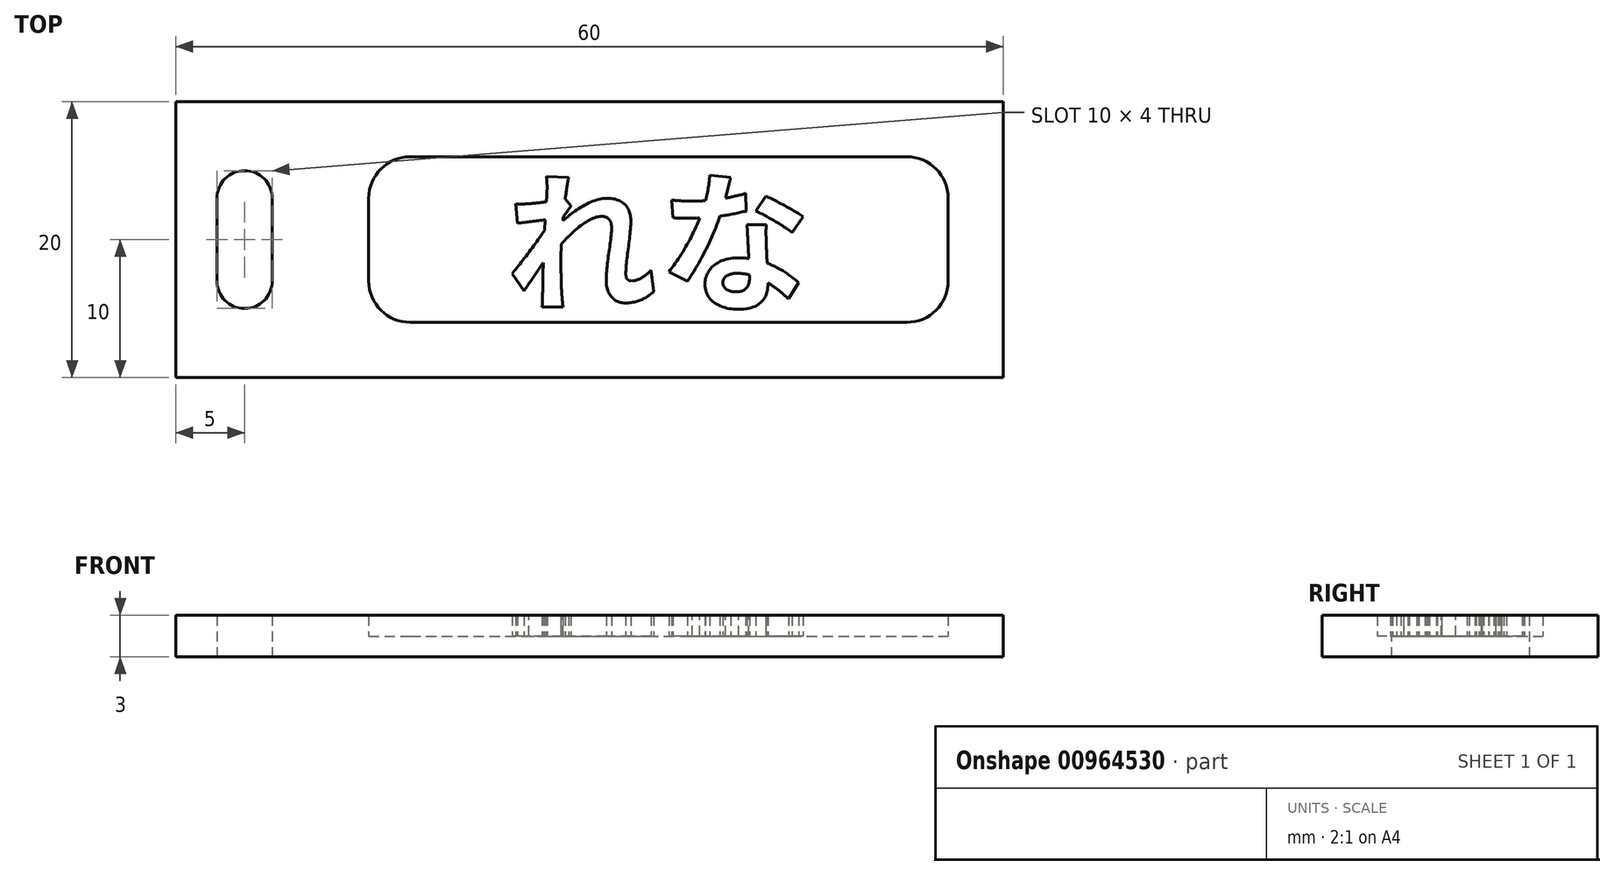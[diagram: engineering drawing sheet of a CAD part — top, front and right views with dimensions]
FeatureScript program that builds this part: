
annotation { "Feature Type Name" : "Feature", "Feature Type Description" : "" }
export const myFeature = defineFeature(function(context is Context, id is Id, definition is map)
    precondition{}
    {
        {
            var Q0;
            Q0=qCreatedBy(makeId("Top.planeOp"),FACE);
            var sketch = newSketch(context, id + "F0", { "sketchPlane" : qUnion([Q0])});
            skLineSegment(sketch, "E0.bottom", {"start": v(-25, 10) * mm, "end": v(25, 10) * mm});
            skLineSegment(sketch, "E0.top", {"start": v(-25, -10) * mm, "end": v(25, -10) * mm});
            skLineSegment(sketch, "E0.left", {"start": v(-25, 10) * mm, "end": v(-25, -10) * mm});
            skLineSegment(sketch, "E0.right", {"start": v(25, 10) * mm, "end": v(25, -10) * mm});
            skPoint(sketch, "E0.middle", {"position": v(0, 0) * mm});
            skLineSegment(sketch, "E1.bottom", {"start": v(-25, 10) * mm, "end": v(-35, 10) * mm});
            skLineSegment(sketch, "E1.top", {"start": v(-25, -10) * mm, "end": v(-35, -10) * mm});
            skLineSegment(sketch, "E1.right", {"start": v(-35, 10) * mm, "end": v(-35, -10) * mm});
            skPoint(sketch, "E1.middle", {"position": v(-30, 0) * mm});
            skLineSegment(sketch, "E2.bottom", {"start": v(-30, 5) * mm, "end": v(-30, 5) * mm});
            skLineSegment(sketch, "E2.top", {"start": v(-30, -5) * mm, "end": v(-30, -5) * mm});
            skLineSegment(sketch, "E2.left", {"start": v(-32, 3) * mm, "end": v(-32, -3) * mm});
            skLineSegment(sketch, "E2.right", {"start": v(-28, 3) * mm, "end": v(-28, -3) * mm});
            skPoint(sketch, "E3.visualSharp", {"position": v(-32, 5) * mm});
            skArc(sketch, "E3.filletArc", {"start": v(-30, 5) * mm, "mid": v(-31.41, 4.41) * mm, "end": v(-32, 3) * mm});
            skPoint(sketch, "E4.visualSharp", {"position": v(-28, 5) * mm});
            skArc(sketch, "E4.filletArc", {"start": v(-28, 3) * mm, "mid": v(-28.59, 4.41) * mm, "end": v(-30, 5) * mm});
            skPoint(sketch, "E5.visualSharp", {"position": v(-28, -5) * mm});
            skArc(sketch, "E5.filletArc", {"start": v(-30, -5) * mm, "mid": v(-28.59, -4.41) * mm, "end": v(-28, -3) * mm});
            skPoint(sketch, "E6.visualSharp", {"position": v(-32, -5) * mm});
            skArc(sketch, "E6.filletArc", {"start": v(-32, -3) * mm, "mid": v(-31.41, -4.41) * mm, "end": v(-30, -5) * mm});
            skSolve(sketch);
        }
        {
            var Q0;
            Q0 = qSketchRegion(id + "F0", true);
            extrude(context, id + "F1", {"entities" : qUnion([Q0]), "depth" : 3 * mm, "offsetDistance" : 25 * mm});
        }
        {
            var Q0;
            Q0=qCreatedBy(makeId("Top.planeOp"),FACE);
            var sketch = newSketch(context, id + "F2", { "sketchPlane" : qUnion([Q0])});
            skLineSegment(sketch, "E7.bottom", {"start": v(-18, -6) * mm, "end": v(18, -6) * mm});
            skLineSegment(sketch, "E7.top", {"start": v(-18, 6) * mm, "end": v(18, 6) * mm});
            skLineSegment(sketch, "E7.left", {"start": v(-21, -3) * mm, "end": v(-21, 3) * mm});
            skLineSegment(sketch, "E7.right", {"start": v(21, -3) * mm, "end": v(21, 3) * mm});
            skPoint(sketch, "E7.middle", {"position": v(0, 0) * mm});
            skPoint(sketch, "E8.visualSharp", {"position": v(-21, 6) * mm});
            skArc(sketch, "E8.filletArc", {"start": v(-18, 6) * mm, "mid": v(-20.12, 5.12) * mm, "end": v(-21, 3) * mm});
            skPoint(sketch, "E9.visualSharp", {"position": v(-21, -6) * mm});
            skArc(sketch, "E9.filletArc", {"start": v(-21, -3) * mm, "mid": v(-20.12, -5.12) * mm, "end": v(-18, -6) * mm});
            skPoint(sketch, "E10.visualSharp", {"position": v(21, -6) * mm});
            skArc(sketch, "E10.filletArc", {"start": v(18, -6) * mm, "mid": v(20.12, -5.12) * mm, "end": v(21, -3) * mm});
            skPoint(sketch, "E11.visualSharp", {"position": v(21, 6) * mm});
            skArc(sketch, "E11.filletArc", {"start": v(21, 3) * mm, "mid": v(20.12, 5.12) * mm, "end": v(18, 6) * mm});
            skSolve(sketch);
        }
        {
            var Q0;
            Q0 = qSketchRegion(id + "F2", true);
            extrude(context, id + "F3", {"entities" : qUnion([Q0]), "depth" : 3 * mm, "offsetDistance" : 25 * mm});
        }
        {
            var Q0;
            Q0=makeQuery(id+"F3.opExtrude","SWEPT_BODY",BODY,{"disambiguationData":[OSD([sQuery(id+"F2.wireOp",EDGE,"E7.bottom"),sQuery(id+"F2.wireOp",EDGE,"E7.top"),sQuery(id+"F2.wireOp",EDGE,"E7.left"),sQuery(id+"F2.wireOp",EDGE,"E7.right"),sQuery(id+"F2.wireOp",EDGE,"E8.filletArc"),sQuery(id+"F2.wireOp",EDGE,"E9.filletArc"),sQuery(id+"F2.wireOp",EDGE,"E10.filletArc"),sQuery(id+"F2.wireOp",EDGE,"E11.filletArc")])]});
            transform(context, id + "F4", {"entities" : qUnion([Q0]), "transformType" : TransformType.TRANSLATION_3D, "dx" : 0 * mm, "dy" : 0 * mm, "dz" : 1.5 * mm, "makeCopy" : false});
        }
        {
            var Q0;
            Q0=makeQuery(id+"F3.opExtrude","SWEPT_BODY",BODY,{"disambiguationData":[OSD([sQuery(id+"F2.wireOp",EDGE,"E7.bottom"),sQuery(id+"F2.wireOp",EDGE,"E7.top"),sQuery(id+"F2.wireOp",EDGE,"E7.left"),sQuery(id+"F2.wireOp",EDGE,"E7.right"),sQuery(id+"F2.wireOp",EDGE,"E8.filletArc"),sQuery(id+"F2.wireOp",EDGE,"E9.filletArc"),sQuery(id+"F2.wireOp",EDGE,"E10.filletArc"),sQuery(id+"F2.wireOp",EDGE,"E11.filletArc")])]});
            var Q1;
            Q1=makeQuery(id+"F1.opExtrude","SWEPT_BODY",BODY,{"disambiguationData":[OSD([sQuery(id+"F0.wireOp",EDGE,"E0.bottom"),sQuery(id+"F0.wireOp",EDGE,"E0.top"),sQuery(id+"F0.wireOp",EDGE,"E0.right"),sQuery(id+"F0.wireOp",EDGE,"E1.bottom"),sQuery(id+"F0.wireOp",EDGE,"E1.top"),sQuery(id+"F0.wireOp",EDGE,"E1.right"),sQuery(id+"F0.wireOp",EDGE,"E2.left"),sQuery(id+"F0.wireOp",EDGE,"E2.right"),sQuery(id+"F0.wireOp",EDGE,"E3.filletArc"),sQuery(id+"F0.wireOp",EDGE,"E4.filletArc"),sQuery(id+"F0.wireOp",EDGE,"E5.filletArc"),sQuery(id+"F0.wireOp",EDGE,"E6.filletArc")])]});
            booleanBodies(context, id + "F5", {"operationType" : BooleanOperationType.SUBTRACTION, "tools" : qUnion([Q0]), "targets" : qUnion([Q1])});
        }
        {
            var Q0;
            Q0=qCreatedBy(makeId("Top.planeOp"),FACE);
            var sketch = newSketch(context, id + "F6", { "sketchPlane" : qUnion([Q0])});
            skText(sketch, "E12", { "text": "れな", "fontName": "NotoSansCJKjp-Bold.otf"});
            const initialGuessF6  = {"E12": [-0.01112, -0.0044, 1, 0, 0.008]};
            skSetInitialGuess(sketch, initialGuessF6);
            skSolve(sketch);
        }
        {
            var Q0;
            Q0 = qSketchRegion(id + "F6", true);
            extrude(context, id + "F7", {"entities" : qUnion([Q0]), "operationType" : NewBodyOperationType.ADD, "depth" : 3 * mm, "offsetDistance" : 25 * mm});
        }
    });
